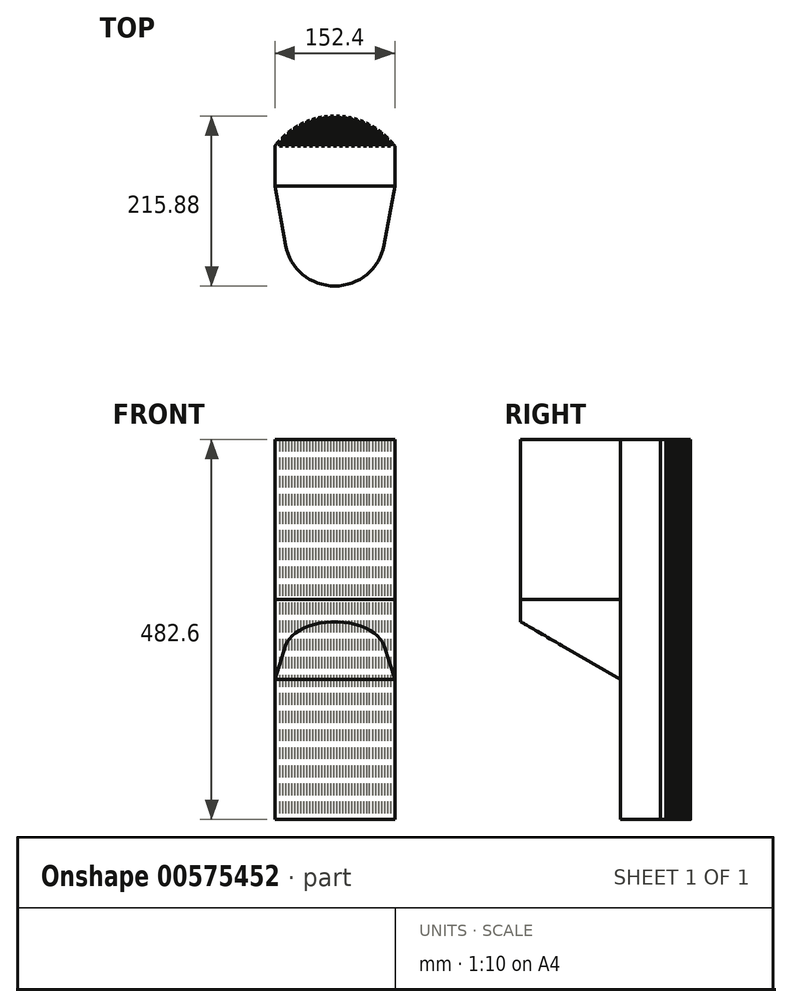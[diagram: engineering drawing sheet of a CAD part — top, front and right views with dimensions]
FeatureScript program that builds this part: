
annotation { "Feature Type Name" : "Feature", "Feature Type Description" : "" }
export const myFeature = defineFeature(function(context is Context, id is Id, definition is map)
    precondition{}
    {
        {
            var Q0;
            Q0=qCreatedBy(makeId("Top.planeOp"),FACE);
            var sketch = newSketch(context, id + "F0", { "sketchPlane" : qUnion([Q0])});
            skLineSegment(sketch, "E0", {"start": v(-76.2, 50.8) * mm, "end": v(-76.2, 0) * mm});
            skLineSegment(sketch, "E1", {"start": v(-76.2, 0) * mm, "end": v(76.2, 0) * mm});
            skLineSegment(sketch, "E2", {"start": v(76.2, 0) * mm, "end": v(76.2, 50.8) * mm});
            skArc(sketch, "E3", {"start": v(76.2, 50.8) * mm, "mid": v(0, 88.9) * mm, "end": v(-76.2, 50.8) * mm});
            skLineSegment(sketch, "E4", {"start": v(0, 88.9) * mm, "end": v(0, 0) * mm, "construction": true});
            skSolve(sketch);
        }
        {
            var Q0;
            Q0=makeQuery(id+"F0.imprint","IMPRINT",FACE,{"disambiguationData":[TD([[makeQuery(id+"F0.imprint","IMPRINT",EDGE,{"derivedFrom":sQuery(id+"F0.wireOp",EDGE,"E0")}),1.0]])]});
            extrude(context, id + "F1", {"entities" : qUnion([Q0]), "depth" : 482.6 * mm, "offsetDistance" : 25.4 * mm});
        }
        {
            var Q0;
            Q0=makeQuery(id+"F1.opExtrude","CAP_FACE",FACE,{"disambiguationData":[OSD([sQuery(id+"F0.wireOp",EDGE,"E0"),sQuery(id+"F0.wireOp",EDGE,"E1"),sQuery(id+"F0.wireOp",EDGE,"E2"),sQuery(id+"F0.wireOp",EDGE,"E3")])],"isStart":false});
            var sketch = newSketch(context, id + "F2", { "sketchPlane" : qUnion([Q0])});
            skLineSegment(sketch, "E5.bottom", {"start": v(-1.9, 88.9) * mm, "end": v(1.9, 88.9) * mm});
            skLineSegment(sketch, "E5.top", {"start": v(-1.9, 50.8) * mm, "end": v(1.9, 50.8) * mm});
            skLineSegment(sketch, "E5.left", {"start": v(-1.9, 88.9) * mm, "end": v(-1.9, 50.8) * mm});
            skLineSegment(sketch, "E5.right", {"start": v(1.9, 88.9) * mm, "end": v(1.9, 50.8) * mm});
            skLineSegment(sketch, "E6.1.0.0", {"start": v(9.52, 88.9) * mm, "end": v(9.52, 50.8) * mm});
            skLineSegment(sketch, "E6.1.0.1", {"start": v(5.71, 88.9) * mm, "end": v(5.71, 50.8) * mm});
            skLineSegment(sketch, "E6.1.0.2", {"start": v(5.71, 50.8) * mm, "end": v(9.52, 50.8) * mm});
            skLineSegment(sketch, "E6.1.0.3", {"start": v(5.71, 88.9) * mm, "end": v(9.52, 88.9) * mm});
            skLineSegment(sketch, "E6.2.0.0", {"start": v(17.14, 88.9) * mm, "end": v(17.14, 50.8) * mm});
            skLineSegment(sketch, "E6.2.0.1", {"start": v(13.33, 88.9) * mm, "end": v(13.33, 50.8) * mm});
            skLineSegment(sketch, "E6.2.0.2", {"start": v(13.33, 50.8) * mm, "end": v(17.14, 50.8) * mm});
            skLineSegment(sketch, "E6.2.0.3", {"start": v(13.33, 88.9) * mm, "end": v(17.14, 88.9) * mm});
            skLineSegment(sketch, "E6.3.0.0", {"start": v(24.76, 88.9) * mm, "end": v(24.76, 50.8) * mm});
            skLineSegment(sketch, "E6.3.0.1", {"start": v(20.95, 88.9) * mm, "end": v(20.95, 50.8) * mm});
            skLineSegment(sketch, "E6.3.0.2", {"start": v(20.95, 50.8) * mm, "end": v(24.76, 50.8) * mm});
            skLineSegment(sketch, "E6.3.0.3", {"start": v(20.95, 88.9) * mm, "end": v(24.76, 88.9) * mm});
            skLineSegment(sketch, "E6.4.0.0", {"start": v(32.38, 88.9) * mm, "end": v(32.38, 50.8) * mm});
            skLineSegment(sketch, "E6.4.0.1", {"start": v(28.57, 88.9) * mm, "end": v(28.57, 50.8) * mm});
            skLineSegment(sketch, "E6.4.0.2", {"start": v(28.57, 50.8) * mm, "end": v(32.38, 50.8) * mm});
            skLineSegment(sketch, "E6.4.0.3", {"start": v(28.57, 88.9) * mm, "end": v(32.38, 88.9) * mm});
            skLineSegment(sketch, "E6.5.0.0", {"start": v(40, 88.9) * mm, "end": v(40, 50.8) * mm});
            skLineSegment(sketch, "E6.5.0.1", {"start": v(36.2, 88.9) * mm, "end": v(36.2, 50.8) * mm});
            skLineSegment(sketch, "E6.5.0.2", {"start": v(36.2, 50.8) * mm, "end": v(40, 50.8) * mm});
            skLineSegment(sketch, "E6.5.0.3", {"start": v(36.2, 88.9) * mm, "end": v(40, 88.9) * mm});
            skLineSegment(sketch, "E6.6.0.0", {"start": v(47.62, 88.9) * mm, "end": v(47.62, 50.8) * mm});
            skLineSegment(sketch, "E6.6.0.1", {"start": v(43.81, 88.9) * mm, "end": v(43.81, 50.8) * mm});
            skLineSegment(sketch, "E6.6.0.2", {"start": v(43.81, 50.8) * mm, "end": v(47.62, 50.8) * mm});
            skLineSegment(sketch, "E6.6.0.3", {"start": v(43.81, 88.9) * mm, "end": v(47.62, 88.9) * mm});
            skLineSegment(sketch, "E6.7.0.0", {"start": v(55.24, 88.9) * mm, "end": v(55.24, 50.8) * mm});
            skLineSegment(sketch, "E6.7.0.1", {"start": v(51.43, 88.9) * mm, "end": v(51.43, 50.8) * mm});
            skLineSegment(sketch, "E6.7.0.2", {"start": v(51.43, 50.8) * mm, "end": v(55.24, 50.8) * mm});
            skLineSegment(sketch, "E6.7.0.3", {"start": v(51.43, 88.9) * mm, "end": v(55.24, 88.9) * mm});
            skLineSegment(sketch, "E6.8.0.0", {"start": v(62.86, 88.9) * mm, "end": v(62.86, 50.8) * mm});
            skLineSegment(sketch, "E6.8.0.1", {"start": v(59.05, 88.9) * mm, "end": v(59.05, 50.8) * mm});
            skLineSegment(sketch, "E6.8.0.2", {"start": v(59.05, 50.8) * mm, "end": v(62.86, 50.8) * mm});
            skLineSegment(sketch, "E6.8.0.3", {"start": v(59.05, 88.9) * mm, "end": v(62.86, 88.9) * mm});
            skLineSegment(sketch, "E6.9.0.0", {"start": v(70.48, 88.9) * mm, "end": v(70.48, 50.8) * mm});
            skLineSegment(sketch, "E6.9.0.1", {"start": v(66.67, 88.9) * mm, "end": v(66.67, 50.8) * mm});
            skLineSegment(sketch, "E6.9.0.2", {"start": v(66.67, 50.8) * mm, "end": v(70.48, 50.8) * mm});
            skLineSegment(sketch, "E6.9.0.3", {"start": v(66.67, 88.9) * mm, "end": v(70.48, 88.9) * mm});
            skLineSegment(sketch, "E6.direction1", {"start": v(-1.9, 50.8) * mm, "end": v(5.71, 50.8) * mm, "construction": true});
            skLineSegment(sketch, "E7.1.0.0", {"start": v(-5.72, 88.9) * mm, "end": v(-5.72, 50.8) * mm});
            skLineSegment(sketch, "E7.1.0.1", {"start": v(-9.53, 88.9) * mm, "end": v(-9.53, 50.8) * mm});
            skLineSegment(sketch, "E7.1.0.2", {"start": v(-9.53, 50.8) * mm, "end": v(-5.72, 50.8) * mm});
            skLineSegment(sketch, "E7.1.0.3", {"start": v(-9.53, 88.9) * mm, "end": v(-5.72, 88.9) * mm});
            skLineSegment(sketch, "E7.2.0.0", {"start": v(-13.34, 88.9) * mm, "end": v(-13.34, 50.8) * mm});
            skLineSegment(sketch, "E7.2.0.1", {"start": v(-17.15, 88.9) * mm, "end": v(-17.15, 50.8) * mm});
            skLineSegment(sketch, "E7.2.0.2", {"start": v(-17.15, 50.8) * mm, "end": v(-13.34, 50.8) * mm});
            skLineSegment(sketch, "E7.2.0.3", {"start": v(-17.15, 88.9) * mm, "end": v(-13.34, 88.9) * mm});
            skLineSegment(sketch, "E7.3.0.0", {"start": v(-20.96, 88.9) * mm, "end": v(-20.96, 50.8) * mm});
            skLineSegment(sketch, "E7.3.0.1", {"start": v(-24.77, 88.9) * mm, "end": v(-24.77, 50.8) * mm});
            skLineSegment(sketch, "E7.3.0.2", {"start": v(-24.77, 50.8) * mm, "end": v(-20.96, 50.8) * mm});
            skLineSegment(sketch, "E7.3.0.3", {"start": v(-24.77, 88.9) * mm, "end": v(-20.96, 88.9) * mm});
            skLineSegment(sketch, "E7.4.0.0", {"start": v(-28.58, 88.9) * mm, "end": v(-28.58, 50.8) * mm});
            skLineSegment(sketch, "E7.4.0.1", {"start": v(-32.39, 88.9) * mm, "end": v(-32.39, 50.8) * mm});
            skLineSegment(sketch, "E7.4.0.2", {"start": v(-32.39, 50.8) * mm, "end": v(-28.58, 50.8) * mm});
            skLineSegment(sketch, "E7.4.0.3", {"start": v(-32.39, 88.9) * mm, "end": v(-28.58, 88.9) * mm});
            skLineSegment(sketch, "E7.5.0.0", {"start": v(-36.2, 88.9) * mm, "end": v(-36.2, 50.8) * mm});
            skLineSegment(sketch, "E7.5.0.1", {"start": v(-40, 88.9) * mm, "end": v(-40, 50.8) * mm});
            skLineSegment(sketch, "E7.5.0.2", {"start": v(-40, 50.8) * mm, "end": v(-36.2, 50.8) * mm});
            skLineSegment(sketch, "E7.5.0.3", {"start": v(-40, 88.9) * mm, "end": v(-36.2, 88.9) * mm});
            skLineSegment(sketch, "E7.6.0.0", {"start": v(-43.82, 88.9) * mm, "end": v(-43.82, 50.8) * mm});
            skLineSegment(sketch, "E7.6.0.1", {"start": v(-47.63, 88.9) * mm, "end": v(-47.63, 50.8) * mm});
            skLineSegment(sketch, "E7.6.0.2", {"start": v(-47.63, 50.8) * mm, "end": v(-43.82, 50.8) * mm});
            skLineSegment(sketch, "E7.6.0.3", {"start": v(-47.63, 88.9) * mm, "end": v(-43.82, 88.9) * mm});
            skLineSegment(sketch, "E7.7.0.0", {"start": v(-51.44, 88.9) * mm, "end": v(-51.44, 50.8) * mm});
            skLineSegment(sketch, "E7.7.0.1", {"start": v(-55.25, 88.9) * mm, "end": v(-55.25, 50.8) * mm});
            skLineSegment(sketch, "E7.7.0.2", {"start": v(-55.25, 50.8) * mm, "end": v(-51.44, 50.8) * mm});
            skLineSegment(sketch, "E7.7.0.3", {"start": v(-55.25, 88.9) * mm, "end": v(-51.44, 88.9) * mm});
            skLineSegment(sketch, "E7.8.0.0", {"start": v(-59.06, 88.9) * mm, "end": v(-59.06, 50.8) * mm});
            skLineSegment(sketch, "E7.8.0.1", {"start": v(-62.87, 88.9) * mm, "end": v(-62.87, 50.8) * mm});
            skLineSegment(sketch, "E7.8.0.2", {"start": v(-62.87, 50.8) * mm, "end": v(-59.06, 50.8) * mm});
            skLineSegment(sketch, "E7.8.0.3", {"start": v(-62.87, 88.9) * mm, "end": v(-59.06, 88.9) * mm});
            skLineSegment(sketch, "E7.9.0.0", {"start": v(-66.68, 88.9) * mm, "end": v(-66.68, 50.8) * mm});
            skLineSegment(sketch, "E7.9.0.1", {"start": v(-70.49, 88.9) * mm, "end": v(-70.49, 50.8) * mm});
            skLineSegment(sketch, "E7.9.0.2", {"start": v(-70.49, 50.8) * mm, "end": v(-66.68, 50.8) * mm});
            skLineSegment(sketch, "E7.9.0.3", {"start": v(-70.49, 88.9) * mm, "end": v(-66.68, 88.9) * mm});
            skLineSegment(sketch, "E7.direction1", {"start": v(-1.9, 50.8) * mm, "end": v(-9.53, 50.8) * mm, "construction": true});
            skSolve(sketch);
        }
        {
            var Q0;
            Q0 = qSketchRegion(id + "F2", true);
            extrude(context, id + "F3", {"entities" : qUnion([Q0]), "operationType" : NewBodyOperationType.REMOVE, "oppositeDirection" : true, "depth" : 482.6 * mm, "offsetDistance" : 25.4 * mm});
        }
        {
            var Q0;
            Q0=makeQuery(id+"F1.opExtrude","CAP_FACE",FACE,{"disambiguationData":[OSD([sQuery(id+"F0.wireOp",EDGE,"E0"),sQuery(id+"F0.wireOp",EDGE,"E1"),sQuery(id+"F0.wireOp",EDGE,"E2"),sQuery(id+"F0.wireOp",EDGE,"E3")])],"isStart":false});
            var sketch = newSketch(context, id + "F4", { "sketchPlane" : qUnion([Q0])});
            skCircle(sketch, "E8", {"center": v(0, -63.5) * mm, "radius": 63.5 * mm});
            skLineSegment(sketch, "E9", {"start": v(-76.2, 0) * mm, "end": v(-62.46, -74.95) * mm});
            skLineSegment(sketch, "E10", {"start": v(76.2, 0) * mm, "end": v(62.46, -74.95) * mm});
            skLineSegment(sketch, "E11", {"start": v(76.2, 0) * mm, "end": v(-76.2, 0) * mm});
            skSolve(sketch);
        }
        {
            var Q0;
            Q0 = qSketchRegion(id + "F4", true);
            extrude(context, id + "F5", {"entities" : qUnion([Q0]), "operationType" : NewBodyOperationType.ADD, "oppositeDirection" : true, "depth" : 304.8 * mm, "offsetDistance" : 25.4 * mm});
        }
        {
            var Q0;
            Q0=makeQuery(id+"F1.opExtrude","SWEPT_FACE",FACE,{"disambiguationData":[OSD([sQuery(id+"F0.wireOp",EDGE,"E2")])]});
            var sketch = newSketch(context, id + "F6", { "sketchPlane" : qUnion([Q0])});
            skLineSegment(sketch, "E12", {"start": v(0, 177.8) * mm, "end": v(-138.08, 257.52) * mm});
            skLineSegment(sketch, "E13", {"start": v(-138.08, 257.52) * mm, "end": v(-138.08, 177.8) * mm});
            skLineSegment(sketch, "E14", {"start": v(-138.08, 177.8) * mm, "end": v(0, 177.8) * mm});
            skLineSegment(sketch, "E15.bottom", {"start": v(0, 482.6) * mm, "end": v(-138.08, 482.6) * mm});
            skLineSegment(sketch, "E15.top", {"start": v(0, 279.4) * mm, "end": v(-138.08, 279.4) * mm});
            skLineSegment(sketch, "E15.left", {"start": v(0, 482.6) * mm, "end": v(0, 279.4) * mm});
            skLineSegment(sketch, "E15.right", {"start": v(-138.08, 482.6) * mm, "end": v(-138.08, 279.4) * mm});
            skSolve(sketch);
        }
        {
            var Q0;
            Q0 = qSketchRegion(id + "F6", true);
            extrude(context, id + "F7", {"entities" : qUnion([Q0]), "operationType" : NewBodyOperationType.REMOVE, "oppositeDirection" : true, "depth" : 254 * mm, "offsetDistance" : 25.4 * mm});
        }
        {
            var Q0;
            Q0=makeQuery(id+"F7.boolean.opBoolean","COPY",FACE,{"derivedFrom":makeQuery(id+"F7.opExtrude","SWEPT_FACE",FACE,{"disambiguationData":[OSD([sQuery(id+"F6.wireOp",EDGE,"E15.top")])]})});
            var sketch = newSketch(context, id + "F8", { "sketchPlane" : qUnion([Q0])});
            skLineSegment(sketch, "E16", {"start": v(-76.2, 0) * mm, "end": v(-62.46, -74.95) * mm});
            skLineSegment(sketch, "E17", {"start": v(-76.2, 0) * mm, "end": v(76.2, 0) * mm});
            skLineSegment(sketch, "E18", {"start": v(76.2, 0) * mm, "end": v(62.46, -74.95) * mm});
            skArc(sketch, "E19", {"start": v(-62.46, -74.95) * mm, "mid": v(0, -127) * mm, "end": v(62.46, -74.95) * mm});
            skSolve(sketch);
        }
        {
            var Q0;
            Q0 = qSketchRegion(id + "F8", true);
            var Q1;
            Q1=makeQuery(id+"F5.boolean.opBoolean","MERGE",FACE,{"derivedFrom":[makeQuery(id+"F1.opExtrude","CAP_FACE",FACE,{"disambiguationData":[OSD([sQuery(id+"F0.wireOp",EDGE,"E0"),sQuery(id+"F0.wireOp",EDGE,"E1"),sQuery(id+"F0.wireOp",EDGE,"E2"),sQuery(id+"F0.wireOp",EDGE,"E3")])],"isStart":false}),makeQuery(id+"F5.opExtrude","CAP_FACE",FACE,{"disambiguationData":[OSD([sQuery(id+"F4.wireOp",EDGE,"E8"),sQuery(id+"F4.wireOp",EDGE,"E9"),sQuery(id+"F4.wireOp",EDGE,"E10"),sQuery(id+"F4.wireOp",EDGE,"E11")])],"isStart":true})]});
            extrude(context, id + "F9", {"entities" : qUnion([Q0]), "endBound" : BoundingType.UP_TO_SURFACE, "depth" : 203.2 * mm, "endBoundEntityFace" : qUnion([Q1]), "offsetDistance" : 25.4 * mm});
        }
    });
